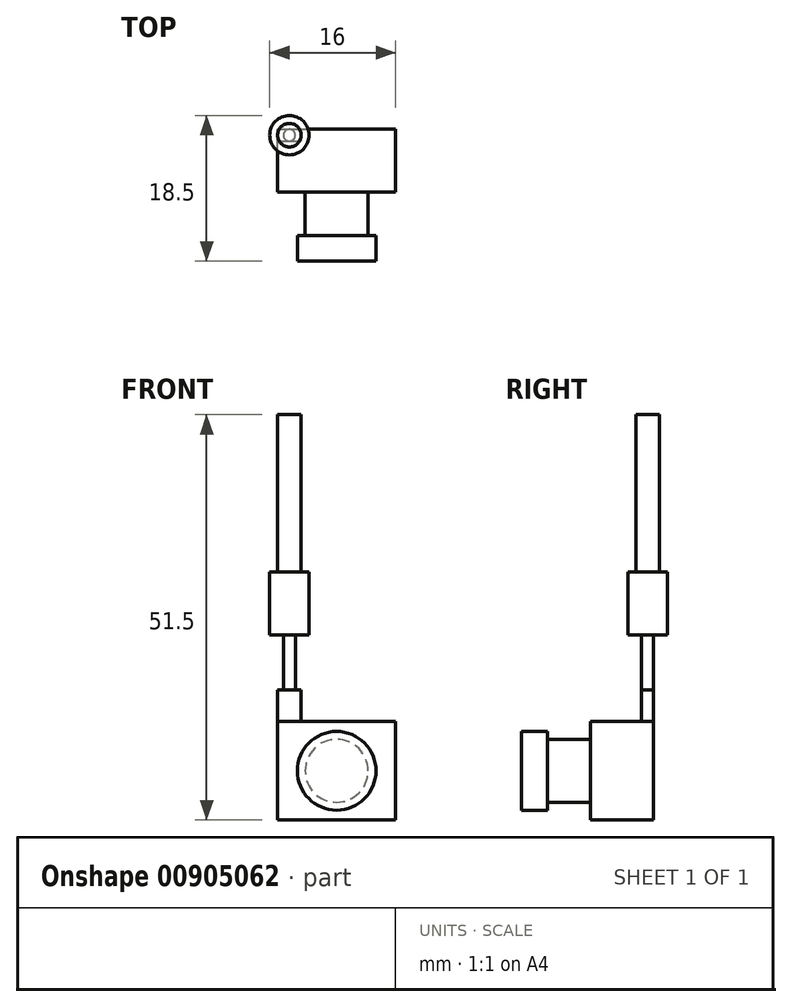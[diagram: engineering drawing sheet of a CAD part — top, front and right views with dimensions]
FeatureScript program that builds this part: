
annotation { "Feature Type Name" : "Feature", "Feature Type Description" : "" }
export const myFeature = defineFeature(function(context is Context, id is Id, definition is map)
    precondition{}
    {
        {
            var Q0;
            Q0=qCreatedBy(makeId("Front.planeOp"),FACE);
            var sketch = newSketch(context, id + "F0", { "sketchPlane" : qUnion([Q0])});
            skLineSegment(sketch, "E0.bottom", {"start": v(0, 0) * mm, "end": v(15, 0) * mm});
            skLineSegment(sketch, "E0.top", {"start": v(0, 12.5) * mm, "end": v(15, 12.5) * mm});
            skLineSegment(sketch, "E0.left", {"start": v(0, 0) * mm, "end": v(0, 12.5) * mm});
            skLineSegment(sketch, "E0.right", {"start": v(15, 0) * mm, "end": v(15, 12.5) * mm});
            skSolve(sketch);
        }
        {
            var Q0;
            Q0=makeQuery(id+"F0.imprint","IMPRINT",FACE,{"disambiguationData":[TD([[makeQuery(id+"F0.imprint","IMPRINT",EDGE,{"derivedFrom":sQuery(id+"F0.wireOp",EDGE,"E0.bottom")}),1.0]])]});
            extrude(context, id + "F1", {"entities" : qUnion([Q0]), "depth" : 8 * mm, "offsetDistance" : 25 * mm});
        }
        {
            var Q0;
            Q0=makeQuery(id+"F1.opExtrude","CAP_FACE",FACE,{"disambiguationData":[OSD([sQuery(id+"F0.wireOp",EDGE,"E0.bottom"),sQuery(id+"F0.wireOp",EDGE,"E0.top"),sQuery(id+"F0.wireOp",EDGE,"E0.left"),sQuery(id+"F0.wireOp",EDGE,"E0.right")])],"isStart":false});
            var sketch = newSketch(context, id + "F2", { "sketchPlane" : qUnion([Q0])});
            skCircle(sketch, "E1", {"center": v(7.5, 6.25) * mm, "radius": 4 * mm});
            skLineSegment(sketch, "E2", {"start": v(0, 6.25) * mm, "end": v(15, 6.25) * mm, "construction": true});
            skSolve(sketch);
        }
        {
            var Q0;
            Q0=makeQuery(id+"F2.imprint","IMPRINT",FACE,{"disambiguationData":[TD([[makeQuery(id+"F2.imprint","IMPRINT",EDGE,{"derivedFrom":sQuery(id+"F2.wireOp",EDGE,"E1")}),1.0]])]});
            extrude(context, id + "F3", {"entities" : qUnion([Q0]), "operationType" : NewBodyOperationType.ADD, "depth" : 5.5 * mm, "offsetDistance" : 25 * mm});
        }
        {
            var Q0;
            Q0=makeQuery(id+"F3.opExtrude","CAP_FACE",FACE,{"disambiguationData":[OSD([sQuery(id+"F2.wireOp",EDGE,"E1")])],"isStart":false});
            var sketch = newSketch(context, id + "F4", { "sketchPlane" : qUnion([Q0])});
            skCircle(sketch, "E3", {"center": v(7.5, 6.25) * mm, "radius": 5 * mm});
            skSolve(sketch);
        }
        {
            var Q0;
            Q0 = qSketchRegion(id + "F4", true);
            extrude(context, id + "F5", {"entities" : qUnion([Q0]), "operationType" : NewBodyOperationType.ADD, "depth" : 3.25 * mm, "offsetDistance" : 25 * mm});
        }
        {
            var Q0;
            Q0=makeQuery(id+"F1.opExtrude","SWEPT_FACE",FACE,{"disambiguationData":[OSD([sQuery(id+"F0.wireOp",EDGE,"E0.top")])]});
            var sketch = newSketch(context, id + "F6", { "sketchPlane" : qUnion([Q0])});
            skLineSegment(sketch, "E4.bottom", {"start": v(0, 0) * mm, "end": v(3, 0) * mm});
            skLineSegment(sketch, "E4.top", {"start": v(0, -1.5) * mm, "end": v(3, -1.5) * mm});
            skLineSegment(sketch, "E4.left", {"start": v(0, 0) * mm, "end": v(0, -1.5) * mm});
            skLineSegment(sketch, "E4.right", {"start": v(3, 0) * mm, "end": v(3, -1.5) * mm});
            skSolve(sketch);
        }
        {
            var Q0;
            Q0 = qSketchRegion(id + "F6", true);
            extrude(context, id + "F7", {"entities" : qUnion([Q0]), "operationType" : NewBodyOperationType.ADD, "depth" : 4 * mm, "offsetDistance" : 25 * mm});
        }
        {
            var Q0;
            Q0=makeQuery(id+"F7.opExtrude","CAP_FACE",FACE,{"disambiguationData":[OSD([sQuery(id+"F6.wireOp",EDGE,"E4.bottom"),sQuery(id+"F6.wireOp",EDGE,"E4.top"),sQuery(id+"F6.wireOp",EDGE,"E4.left"),sQuery(id+"F6.wireOp",EDGE,"E4.right")])],"isStart":false});
            var sketch = newSketch(context, id + "F8", { "sketchPlane" : qUnion([Q0])});
            skCircle(sketch, "E5", {"center": v(1.5, -0.75) * mm, "radius": 0.75 * mm});
            skPoint(sketch, "E5.centerSnap0", {"position": v(1.5, 0) * mm});
            skSolve(sketch);
        }
        {
            var Q0;
            Q0 = qSketchRegion(id + "F8", true);
            extrude(context, id + "F9", {"entities" : qUnion([Q0]), "operationType" : NewBodyOperationType.ADD, "depth" : 7 * mm, "offsetDistance" : 25 * mm});
        }
        {
            var Q0;
            Q0=makeQuery(id+"F9.opExtrude","CAP_FACE",FACE,{"disambiguationData":[OSD([sQuery(id+"F8.wireOp",EDGE,"E5")])],"isStart":false});
            var sketch = newSketch(context, id + "F10", { "sketchPlane" : qUnion([Q0])});
            skCircle(sketch, "E6", {"center": v(1.5, -0.75) * mm, "radius": 2.5 * mm});
            skSolve(sketch);
        }
        {
            var Q0;
            Q0 = qSketchRegion(id + "F10", true);
            extrude(context, id + "F11", {"entities" : qUnion([Q0]), "operationType" : NewBodyOperationType.ADD, "depth" : 8 * mm, "offsetDistance" : 25 * mm});
        }
        {
            var Q0;
            Q0=makeQuery(id+"F11.opExtrude","CAP_FACE",FACE,{"disambiguationData":[OSD([sQuery(id+"F10.wireOp",EDGE,"E6")])],"isStart":false});
            var sketch = newSketch(context, id + "F12", { "sketchPlane" : qUnion([Q0])});
            skCircle(sketch, "E7", {"center": v(1.5, -0.75) * mm, "radius": 1.5 * mm});
            skSolve(sketch);
        }
        {
            var Q0;
            Q0 = qSketchRegion(id + "F12", true);
            extrude(context, id + "F13", {"entities" : qUnion([Q0]), "operationType" : NewBodyOperationType.ADD, "depth" : 20 * mm, "offsetDistance" : 25 * mm});
        }
    });
